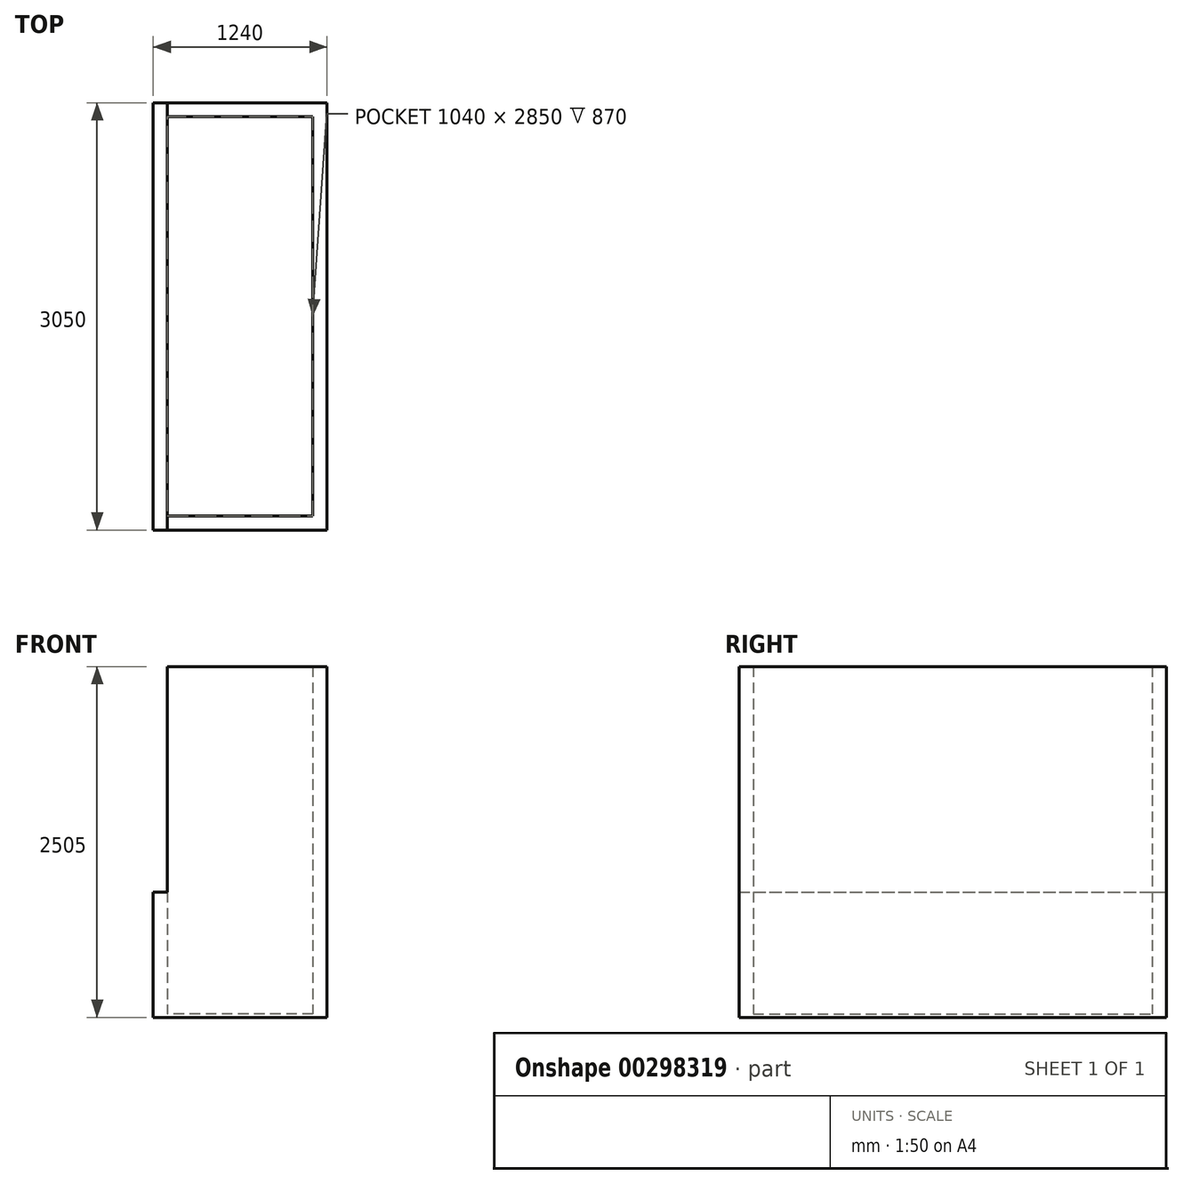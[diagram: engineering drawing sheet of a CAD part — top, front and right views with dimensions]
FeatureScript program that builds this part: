
annotation { "Feature Type Name" : "Feature", "Feature Type Description" : "" }
export const myFeature = defineFeature(function(context is Context, id is Id, definition is map)
    precondition{}
    {
        {
            var Q0;
            Q0=qCreatedBy(makeId("Top.planeOp"),FACE);
            var sketch = newSketch(context, id + "F0", { "sketchPlane" : qUnion([Q0])});
            skLineSegment(sketch, "E0.bottom", {"start": v(520, -1425) * mm, "end": v(-520, -1425) * mm});
            skLineSegment(sketch, "E0.top", {"start": v(520, 1425) * mm, "end": v(-520, 1425) * mm});
            skLineSegment(sketch, "E0.left", {"start": v(520, -1425) * mm, "end": v(520, 1425) * mm});
            skLineSegment(sketch, "E0.right", {"start": v(-520, -1425) * mm, "end": v(-520, 1425) * mm});
            skPoint(sketch, "E0.middle", {"position": v(0, 0) * mm});
            skLineSegment(sketch, "E1.0", {"start": v(-620, -1525) * mm, "end": v(-620, 1525) * mm});
            skLineSegment(sketch, "E1.1", {"start": v(620, -1525) * mm, "end": v(-620, -1525) * mm});
            skLineSegment(sketch, "E1.2", {"start": v(620, -1525) * mm, "end": v(620, 1525) * mm});
            skLineSegment(sketch, "E1.3", {"start": v(620, 1525) * mm, "end": v(-620, 1525) * mm});
            skLineSegment(sketch, "E2", {"start": v(-520, 1425) * mm, "end": v(-520, 1525) * mm});
            skLineSegment(sketch, "E3", {"start": v(-520, -1425) * mm, "end": v(-520, -1525) * mm});
            skSolve(sketch);
        }
        {
            var Q0;
            Q0=makeQuery(id+"F0.imprint","IMPRINT",FACE,{"disambiguationData":[TD([[makeQuery(id+"F0.imprint","IMPRINT",EDGE,{"derivedFrom":sQuery(id+"F0.wireOp",EDGE,"E0.right")}),1.0]])]});
            extrude(context, id + "F1", {"entities" : qUnion([Q0]), "depth" : 870 * mm});
        }
        {
            var Q0;
            Q0=makeQuery(id+"F0.imprint","IMPRINT",FACE,{"disambiguationData":[TD([[makeQuery(id+"F0.imprint","IMPRINT",EDGE,{"derivedFrom":sQuery(id+"F0.wireOp",EDGE,"E0.bottom")}),1.0]])]});
            extrude(context, id + "F2", {"entities" : qUnion([Q0]), "operationType" : NewBodyOperationType.ADD, "depth" : 2480 * mm});
        }
        {
            var Q0;
            Q0=makeQuery(id+"F0.imprint","IMPRINT",FACE,{"disambiguationData":[TD([[makeQuery(id+"F0.imprint","IMPRINT",EDGE,{"derivedFrom":sQuery(id+"F0.wireOp",EDGE,"E0.bottom")}),-1.0]])]});
            var Q1;
            Q1=makeQuery(id+"F0.imprint","IMPRINT",FACE,{"disambiguationData":[TD([[makeQuery(id+"F0.imprint","IMPRINT",EDGE,{"derivedFrom":sQuery(id+"F0.wireOp",EDGE,"E0.right")}),1.0]])]});
            var Q2;
            Q2=makeQuery(id+"F0.imprint","IMPRINT",FACE,{"disambiguationData":[TD([[makeQuery(id+"F0.imprint","IMPRINT",EDGE,{"derivedFrom":sQuery(id+"F0.wireOp",EDGE,"E0.bottom")}),1.0]])]});
            extrude(context, id + "F3", {"entities" : qUnion([Q0, Q1, Q2]), "operationType" : NewBodyOperationType.ADD, "oppositeDirection" : true, "depth" : 25 * mm});
        }
    });
